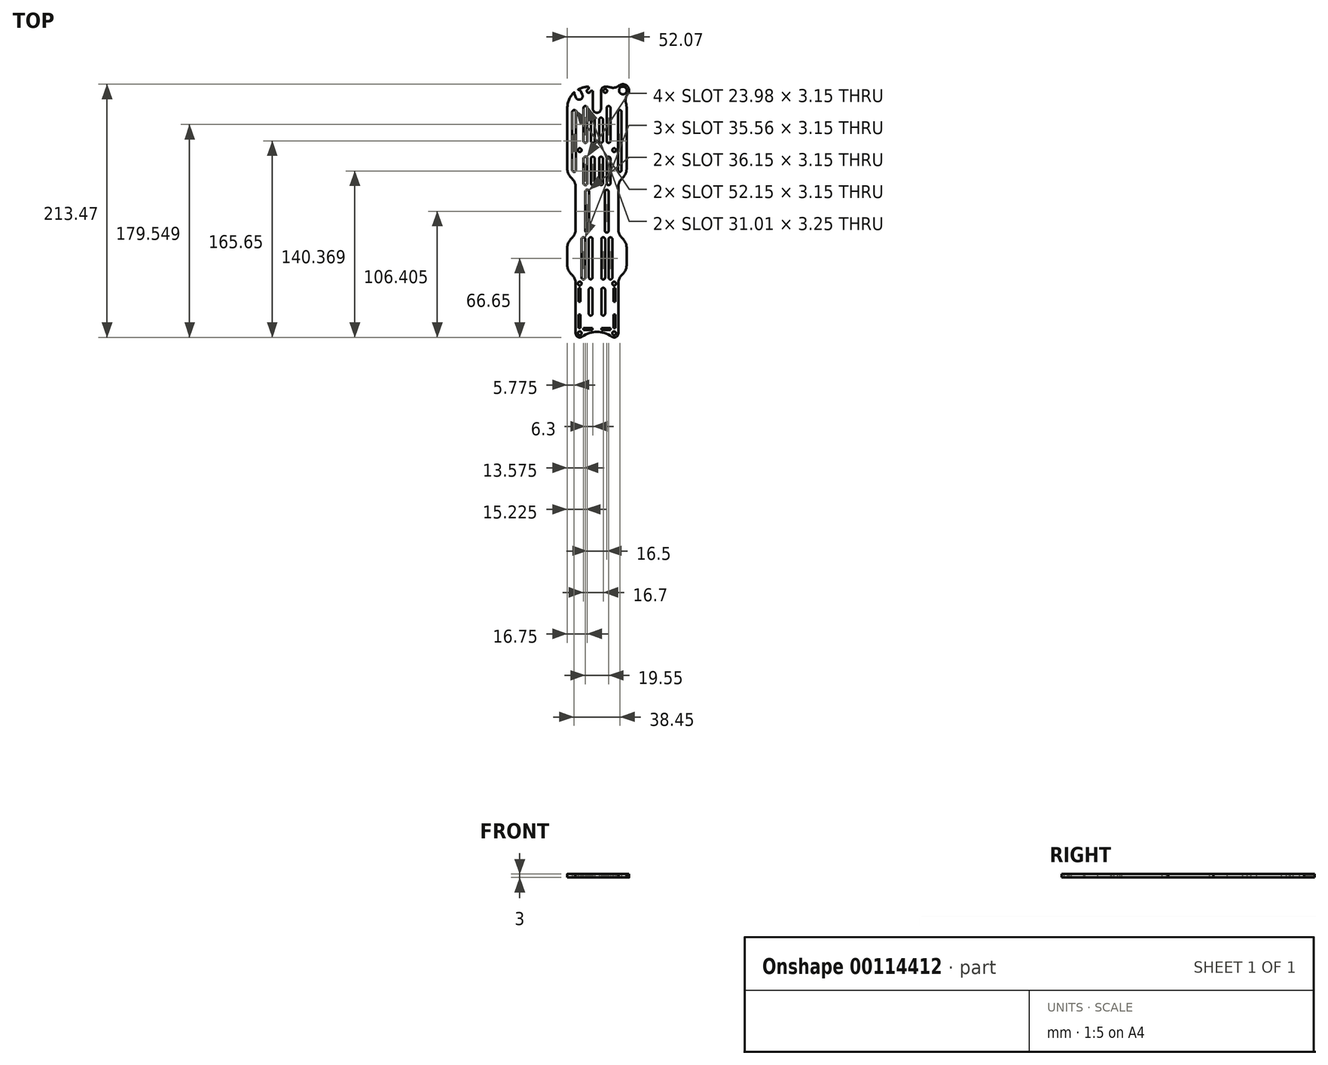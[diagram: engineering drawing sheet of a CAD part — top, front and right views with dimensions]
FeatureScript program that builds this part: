
annotation { "Feature Type Name" : "Feature", "Feature Type Description" : "" }
export const myFeature = defineFeature(function(context is Context, id is Id, definition is map)
    precondition{}
    {
        {
            var Q0;
            Q0=qCreatedBy(makeId("Top.planeOp"),FACE);
            var sketch = newSketch(context, id + "F0", { "sketchPlane" : qUnion([Q0])});
            skLineSegment(sketch, "E0.bottom", {"start": v(16.5, 48.3) * mm, "end": v(0, 48.3) * mm});
            skLineSegment(sketch, "E0.top", {"start": v(16.5, 15.3) * mm, "end": v(0, 15.3) * mm});
            skLineSegment(sketch, "E0.left", {"start": v(16.5, 48.3) * mm, "end": v(16.5, 15.3) * mm});
            skLineSegment(sketch, "E1", {"start": v(25, 118.8) * mm, "end": v(25, 67.6) * mm});
            skLineSegment(sketch, "E2", {"start": v(0, 31.8) * mm, "end": v(16.5, 48.3) * mm});
            skLineSegment(sketch, "E3", {"start": v(0, 31.8) * mm, "end": v(16.5, 15.3) * mm});
            skLineSegment(sketch, "E4.bottom", {"start": v(0, -66.61) * mm, "end": v(14, -66.61) * mm});
            skLineSegment(sketch, "E4.right", {"start": v(14, -66.61) * mm, "end": v(14, -33.16) * mm});
            skLineSegment(sketch, "E5", {"start": v(14, -33.16) * mm, "end": v(15.65, -33.16) * mm});
            skLineSegment(sketch, "E6", {"start": v(15.65, -33.16) * mm, "end": v(15.65, -44.46) * mm});
            skLineSegment(sketch, "E7", {"start": v(15.65, -44.46) * mm, "end": v(14, -44.46) * mm});
            skLineSegment(sketch, "E8", {"start": v(3.78, -66.61) * mm, "end": v(3.78, -68.26) * mm});
            skLineSegment(sketch, "E9", {"start": v(3.78, -68.26) * mm, "end": v(11.43, -68.26) * mm});
            skLineSegment(sketch, "E10", {"start": v(11.43, -68.26) * mm, "end": v(11.43, -66.61) * mm});
            skLineSegment(sketch, "E11", {"start": v(14, -55.31) * mm, "end": v(15.65, -55.31) * mm});
            skLineSegment(sketch, "E12", {"start": v(14, -66.61) * mm, "end": v(15.65, -66.61) * mm});
            skLineSegment(sketch, "E13", {"start": v(15.65, -66.61) * mm, "end": v(15.65, -55.31) * mm});
            skLineSegment(sketch, "E14", {"start": v(14.5, -66.61) * mm, "end": v(14.5, -71.11) * mm});
            skCircle(sketch, "E15", {"center": v(14.5, -71.11) * mm, "radius": 1.57 * mm});
            skCircle(sketch, "E16", {"center": v(14.5, -29.26) * mm, "radius": 1.57 * mm});
            skCircle(sketch, "E17.MirrorC", {"center": v(7, 133.2) * mm, "radius": 1.57 * mm});
            skCircle(sketch, "E18", {"center": v(14.5, 83.3) * mm, "radius": 1.57 * mm});
            skArc(sketch, "E19", {"start": v(12.45, -73.95) * mm, "mid": v(16.1, -74.23) * mm, "end": v(18, -71.11) * mm});
            skLineSegment(sketch, "E20.trimOffspring", {"start": v(12.93, -71.11) * mm, "end": v(14.5, -71.11) * mm});
            skArc(sketch, "E21", {"start": v(12.45, -73.95) * mm, "mid": v(6.54, -70.96) * mm, "end": v(0, -69.93) * mm});
            skLineSegment(sketch, "E22", {"start": v(14.5, -71.11) * mm, "end": v(18, -71.11) * mm});
            skLineSegment(sketch, "E23", {"start": v(18, -71.11) * mm, "end": v(18, -29.26) * mm});
            skLineSegment(sketch, "E24.trimOffspring", {"start": v(14.5, -30.84) * mm, "end": v(14.5, -29.26) * mm});
            skLineSegment(sketch, "E25", {"start": v(7, 133.2) * mm, "end": v(7, 136.8) * mm});
            skLineSegment(sketch, "E26", {"start": v(7, 133.2) * mm, "end": v(7, 131.63) * mm});
            skArc(sketch, "E27", {"start": v(7, 136.8) * mm, "mid": v(4.46, 135.74) * mm, "end": v(3.4, 133.2) * mm});
            skLineSegment(sketch, "E28.trimOffspring", {"start": v(3.4, 133.2) * mm, "end": v(7, 133.2) * mm});
            skLineSegment(sketch, "E29", {"start": v(3.4, 133.2) * mm, "end": v(3.4, 118.2) * mm});
            skArc(sketch, "E30", {"start": v(0, 114.8) * mm, "mid": v(2.4, 115.8) * mm, "end": v(3.4, 118.2) * mm});
            skLineSegment(sketch, "E31.trimOffspring", {"start": v(0, 114.8) * mm, "end": v(0, -66.61) * mm});
            skArc(sketch, "E32", {"start": v(25, 118.8) * mm, "mid": v(24.85, 121.15) * mm, "end": v(24.38, 123.46) * mm});
            skLineSegment(sketch, "E33", {"start": v(14.5, -29.26) * mm, "end": v(16.07, -29.26) * mm});
            skArc(sketch, "E34", {"start": v(18, -29.26) * mm, "mid": v(18.92, -24.99) * mm, "end": v(21.5, -21.46) * mm});
            skArc(sketch, "E35", {"start": v(21.5, -21.46) * mm, "mid": v(24.08, -17.94) * mm, "end": v(25, -13.66) * mm});
            skLineSegment(sketch, "E36", {"start": v(25, -13.66) * mm, "end": v(25, 1) * mm});
            skArc(sketch, "E37", {"start": v(25, 1) * mm, "mid": v(24.08, 5.27) * mm, "end": v(21.5, 8.8) * mm});
            skArc(sketch, "E38", {"start": v(21.5, 8.8) * mm, "mid": v(19.18, 11.74) * mm, "end": v(18, 15.3) * mm});
            skArc(sketch, "E39", {"start": v(25, 67.6) * mm, "mid": v(24.08, 63.32) * mm, "end": v(21.5, 59.8) * mm});
            skArc(sketch, "E40", {"start": v(21.5, 59.8) * mm, "mid": v(19.18, 56.85) * mm, "end": v(18, 53.3) * mm});
            skLineSegment(sketch, "E41.trimOffspring", {"start": v(14.5, 48.3) * mm, "end": v(14.5, 84.87) * mm});
            skLineSegment(sketch, "E42.trimOffspring", {"start": v(18, 15.3) * mm, "end": v(18, 53.3) * mm});
            skLineSegment(sketch, "E43", {"start": v(5.05, 109.08) * mm, "end": v(5.05, 91) * mm});
            skLineSegment(sketch, "E44", {"start": v(1.9, 109.08) * mm, "end": v(1.9, 91) * mm});
            skLineSegment(sketch, "E45", {"start": v(20.8, 66.54) * mm, "end": v(17.65, 66.54) * mm});
            skCircle(sketch, "E46", {"center": v(19.22, 66.54) * mm, "radius": 1.58 * mm});
            skLineSegment(sketch, "E47", {"start": v(14.5, -29.26) * mm, "end": v(0, -29.26) * mm});
            skLineSegment(sketch, "E48", {"start": v(20.8, 66.54) * mm, "end": v(20.8, 115.54) * mm});
            skLineSegment(sketch, "E49", {"start": v(17.65, 66.54) * mm, "end": v(17.65, 115.54) * mm});
            skLineSegment(sketch, "E50", {"start": v(11.35, 62.93) * mm, "end": v(11.35, 76.17) * mm});
            skLineSegment(sketch, "E51", {"start": v(8.2, 62.93) * mm, "end": v(8.2, 76.17) * mm});
            skLineSegment(sketch, "E52", {"start": v(20.8, 115.54) * mm, "end": v(17.65, 115.54) * mm});
            skLineSegment(sketch, "E53", {"start": v(6.85, -54.61) * mm, "end": v(6.85, -34.36) * mm});
            skLineSegment(sketch, "E54", {"start": v(3.7, -54.61) * mm, "end": v(3.7, -34.36) * mm});
            skLineSegment(sketch, "E55.trimOffspring", {"start": v(3.7, -54.61) * mm, "end": v(6.85, -54.61) * mm});
            skCircle(sketch, "E56", {"center": v(5.28, -54.61) * mm, "radius": 1.57 * mm});
            skLineSegment(sketch, "E57", {"start": v(3.7, 8.24) * mm, "end": v(6.85, 8.24) * mm});
            skCircle(sketch, "E58", {"center": v(5.28, 8.24) * mm, "radius": 1.57 * mm});
            skLineSegment(sketch, "E59.trimOffspring", {"start": v(8.2, 91) * mm, "end": v(11.35, 91) * mm});
            skLineSegment(sketch, "E60.trimOffspring", {"start": v(1.9, 91) * mm, "end": v(5.05, 91) * mm});
            skPoint(sketch, "E61", {"position": v(3.47, 91) * mm});
            skPoint(sketch, "E62", {"position": v(9.77, 91) * mm});
            skCircle(sketch, "E63", {"center": v(3.47, 91) * mm, "radius": 1.58 * mm});
            skLineSegment(sketch, "E64.trimOffspring", {"start": v(1.9, 76.17) * mm, "end": v(1.9, 62.93) * mm});
            skLineSegment(sketch, "E65.trimOffspring", {"start": v(5.05, 76.17) * mm, "end": v(5.05, 62.93) * mm});
            skLineSegment(sketch, "E66.trimOffspring", {"start": v(8.2, 91) * mm, "end": v(8.2, 119.29) * mm});
            skLineSegment(sketch, "E67.trimOffspring", {"start": v(11.35, 91) * mm, "end": v(11.35, 119.29) * mm});
            skCircle(sketch, "E68", {"center": v(9.77, 91) * mm, "radius": 1.57 * mm});
            skCircle(sketch, "E69", {"center": v(19.22, 115.54) * mm, "radius": 1.57 * mm});
            skLineSegment(sketch, "E70.MirrorCS", {"start": v(13, 8.24) * mm, "end": v(13, -24.16) * mm});
            skLineSegment(sketch, "E71.MirrorCS", {"start": v(9.85, 8.24) * mm, "end": v(9.85, -24.16) * mm});
            skLineSegment(sketch, "E72.trimOffspring", {"start": v(0, 1) * mm, "end": v(25, 1) * mm});
            skLineSegment(sketch, "E73.trimOffspring", {"start": v(0, -13.66) * mm, "end": v(25, -13.66) * mm});
            skLineSegment(sketch, "E74.trimOffspring", {"start": v(0, -33.16) * mm, "end": v(14, -33.16) * mm});
            skLineSegment(sketch, "E75", {"start": v(1.9, 109.08) * mm, "end": v(5.05, 109.08) * mm});
            skCircle(sketch, "E76", {"center": v(3.47, 109.08) * mm, "radius": 1.57 * mm});
            skLineSegment(sketch, "E77", {"start": v(8.2, 118.8) * mm, "end": v(11.35, 118.8) * mm});
            skCircle(sketch, "E78", {"center": v(9.77, 118.8) * mm, "radius": 1.65 * mm});
            skLineSegment(sketch, "E79", {"start": v(8.2, 76.17) * mm, "end": v(11.35, 76.17) * mm});
            skLineSegment(sketch, "E80", {"start": v(5.05, 76.17) * mm, "end": v(1.9, 76.17) * mm});
            skCircle(sketch, "E81", {"center": v(3.47, 76.17) * mm, "radius": 1.58 * mm});
            skCircle(sketch, "E82", {"center": v(9.77, 76.17) * mm, "radius": 1.57 * mm});
            skLineSegment(sketch, "E83", {"start": v(5.05, 62.93) * mm, "end": v(5.05, 55.35) * mm});
            skLineSegment(sketch, "E84", {"start": v(8.2, 55.35) * mm, "end": v(11.35, 55.35) * mm});
            skLineSegment(sketch, "E85", {"start": v(5.05, 55.35) * mm, "end": v(1.9, 55.35) * mm});
            skLineSegment(sketch, "E86", {"start": v(1.9, 62.93) * mm, "end": v(1.9, 55.35) * mm});
            skLineSegment(sketch, "E87", {"start": v(11.35, 62.93) * mm, "end": v(11.35, 55.35) * mm});
            skLineSegment(sketch, "E88", {"start": v(8.2, 62.93) * mm, "end": v(8.2, 55.35) * mm});
            skCircle(sketch, "E89", {"center": v(9.77, 55.35) * mm, "radius": 1.57 * mm});
            skCircle(sketch, "E90", {"center": v(3.47, 55.35) * mm, "radius": 1.58 * mm});
            skLineSegment(sketch, "E91.MirrorCS", {"start": v(-12.92, -71.11) * mm, "end": v(-14.5, -71.11) * mm});
            skLineSegment(sketch, "E92.MirrorCS", {"start": v(-7, 133.2) * mm, "end": v(-7, 136.8) * mm});
            skLineSegment(sketch, "E93.MirrorCS", {"start": v(-14.5, -71.11) * mm, "end": v(-18, -71.11) * mm});
            skCircle(sketch, "E94.MirrorC", {"center": v(-14.5, -71.11) * mm, "radius": 1.57 * mm});
            skLineSegment(sketch, "E95.MirrorCS", {"start": v(-14.5, -66.61) * mm, "end": v(-14.5, -71.11) * mm});
            skLineSegment(sketch, "E96.MirrorCS", {"start": v(-14, -33.16) * mm, "end": v(-15.65, -33.16) * mm});
            skLineSegment(sketch, "E97.MirrorCS", {"start": v(-14, -66.61) * mm, "end": v(-15.65, -66.61) * mm});
            skLineSegment(sketch, "E98.MirrorCS", {"start": v(-11.42, -68.26) * mm, "end": v(-11.42, -66.61) * mm});
            skLineSegment(sketch, "E99.MirrorCS", {"start": v(-3.4, 133.2) * mm, "end": v(-7, 133.2) * mm});
            skArc(sketch, "E100.MirrorCS", {"start": v(-12.45, -73.95) * mm, "mid": v(-16.1, -74.23) * mm, "end": v(-18, -71.11) * mm});
            skArc(sketch, "E101.MirrorCS", {"start": v(-7, 136.8) * mm, "mid": v(-4.46, 135.74) * mm, "end": v(-3.4, 133.2) * mm});
            skLineSegment(sketch, "E102.MirrorCS", {"start": v(-7, 133.2) * mm, "end": v(-7, 131.63) * mm});
            skLineSegment(sketch, "E103.MirrorCS", {"start": v(-14.5, -29.26) * mm, "end": v(-16.07, -29.26) * mm});
            skLineSegment(sketch, "E104.MirrorCS", {"start": v(-14.5, -30.84) * mm, "end": v(-14.5, -29.26) * mm});
            skCircle(sketch, "E105.MirrorC", {"center": v(-7, 133.2) * mm, "radius": 1.57 * mm});
            skLineSegment(sketch, "E106.MirrorCS", {"start": v(-8.2, 118.8) * mm, "end": v(-11.35, 118.8) * mm});
            skCircle(sketch, "E107.MirrorC", {"center": v(-14.5, -29.26) * mm, "radius": 1.57 * mm});
            skLineSegment(sketch, "E108.MirrorCS", {"start": v(-3.7, -54.61) * mm, "end": v(-6.85, -54.61) * mm});
            skLineSegment(sketch, "E109.MirrorCS", {"start": v(-3.4, 133.2) * mm, "end": v(-3.4, 118.2) * mm});
            skLineSegment(sketch, "E110.MirrorCS", {"start": v(-1.9, 91) * mm, "end": v(-5.05, 91) * mm});
            skLineSegment(sketch, "E111.MirrorCS", {"start": v(-20.8, 66.54) * mm, "end": v(-17.65, 66.54) * mm});
            skLineSegment(sketch, "E112.MirrorCS", {"start": v(-8.2, 91) * mm, "end": v(-11.35, 91) * mm});
            skCircle(sketch, "E113.MirrorC", {"center": v(-9.77, 118.8) * mm, "radius": 1.65 * mm});
            skLineSegment(sketch, "E114.MirrorCS", {"start": v(-3.7, 8.24) * mm, "end": v(-6.85, 8.24) * mm});
            skLineSegment(sketch, "E115.MirrorCS", {"start": v(-5.05, 55.35) * mm, "end": v(-1.9, 55.35) * mm});
            skCircle(sketch, "E116.MirrorC", {"center": v(-5.27, -54.61) * mm, "radius": 1.57 * mm});
            skLineSegment(sketch, "E117.MirrorCS", {"start": v(-8.2, 55.35) * mm, "end": v(-11.35, 55.35) * mm});
            skCircle(sketch, "E118.MirrorC", {"center": v(-3.47, 91) * mm, "radius": 1.58 * mm});
            skArc(sketch, "E119.MirrorCS", {"start": v(-12.45, -73.95) * mm, "mid": v(-6.54, -70.96) * mm, "end": v(0, -69.93) * mm});
            skCircle(sketch, "E120.MirrorC", {"center": v(-19.22, 66.54) * mm, "radius": 1.58 * mm});
            skArc(sketch, "E121.MirrorCS", {"start": v(-21.5, 8.8) * mm, "mid": v(-19.18, 11.74) * mm, "end": v(-18, 15.3) * mm});
            skLineSegment(sketch, "E122.MirrorCS", {"start": v(-5.05, 62.93) * mm, "end": v(-5.05, 55.35) * mm});
            skLineSegment(sketch, "E123.MirrorCS", {"start": v(-3.77, -68.26) * mm, "end": v(-11.42, -68.26) * mm});
            skLineSegment(sketch, "E124.MirrorCS", {"start": v(-3.77, -66.61) * mm, "end": v(-3.77, -68.26) * mm});
            skLineSegment(sketch, "E125.MirrorCS", {"start": v(0, -66.61) * mm, "end": v(-14, -66.61) * mm});
            skCircle(sketch, "E126.MirrorC", {"center": v(-9.77, 55.35) * mm, "radius": 1.57 * mm});
            skArc(sketch, "E127.MirrorCS", {"start": v(-25, 1) * mm, "mid": v(-24.08, 5.27) * mm, "end": v(-21.5, 8.8) * mm});
            skLineSegment(sketch, "E128.MirrorCS", {"start": v(-8.2, 62.93) * mm, "end": v(-8.2, 55.35) * mm});
            skArc(sketch, "E129.MirrorCS", {"start": v(-18, -29.26) * mm, "mid": v(-18.92, -24.99) * mm, "end": v(-21.5, -21.46) * mm});
            skLineSegment(sketch, "E130.MirrorCS", {"start": v(-8.2, 76.17) * mm, "end": v(-11.35, 76.17) * mm});
            skLineSegment(sketch, "E131.MirrorCS", {"start": v(-5.05, 76.17) * mm, "end": v(-1.9, 76.17) * mm});
            skLineSegment(sketch, "E132.MirrorCS", {"start": v(-11.35, 62.93) * mm, "end": v(-11.35, 55.35) * mm});
            skCircle(sketch, "E133.MirrorC", {"center": v(-9.77, 91) * mm, "radius": 1.57 * mm});
            skCircle(sketch, "E134.MirrorC", {"center": v(-5.27, 8.24) * mm, "radius": 1.57 * mm});
            skArc(sketch, "E135.MirrorCS", {"start": v(-21.5, 59.8) * mm, "mid": v(-19.18, 56.85) * mm, "end": v(-18, 53.3) * mm});
            skArc(sketch, "E136.MirrorCS", {"start": v(0, 114.8) * mm, "mid": v(-2.4, 115.8) * mm, "end": v(-3.4, 118.2) * mm});
            skArc(sketch, "E137.MirrorCS", {"start": v(-25, 67.6) * mm, "mid": v(-24.08, 63.32) * mm, "end": v(-21.5, 59.8) * mm});
            skLineSegment(sketch, "E138.MirrorCS", {"start": v(-1.9, 109.08) * mm, "end": v(-5.05, 109.08) * mm});
            skLineSegment(sketch, "E139.MirrorCS", {"start": v(-15.65, -66.61) * mm, "end": v(-15.65, -55.31) * mm});
            skCircle(sketch, "E140.MirrorC", {"center": v(-3.47, 55.35) * mm, "radius": 1.58 * mm});
            skLineSegment(sketch, "E141.MirrorCS", {"start": v(-15.65, -44.46) * mm, "end": v(-14, -44.46) * mm});
            skLineSegment(sketch, "E142.MirrorCS", {"start": v(-15.65, -33.16) * mm, "end": v(-15.65, -44.46) * mm});
            skLineSegment(sketch, "E143.MirrorCS", {"start": v(-14, -66.61) * mm, "end": v(-14, -33.16) * mm});
            skLineSegment(sketch, "E144.MirrorCS", {"start": v(-14, -55.31) * mm, "end": v(-15.65, -55.31) * mm});
            skCircle(sketch, "E145.MirrorC", {"center": v(-9.77, 76.17) * mm, "radius": 1.57 * mm});
            skArc(sketch, "E146.MirrorCS", {"start": v(-21.5, -21.46) * mm, "mid": v(-24.08, -17.94) * mm, "end": v(-25, -13.66) * mm});
            skCircle(sketch, "E147.MirrorC", {"center": v(-3.47, 76.17) * mm, "radius": 1.58 * mm});
            skLineSegment(sketch, "E148.MirrorCS", {"start": v(-25, -13.66) * mm, "end": v(-25, 1) * mm});
            skLineSegment(sketch, "E149.MirrorCS", {"start": v(-20.8, 115.54) * mm, "end": v(-17.65, 115.54) * mm});
            skCircle(sketch, "E150.MirrorC", {"center": v(-19.22, 115.54) * mm, "radius": 1.57 * mm});
            skCircle(sketch, "E151.MirrorC", {"center": v(-14.5, 83.3) * mm, "radius": 1.57 * mm});
            skLineSegment(sketch, "E152.MirrorCS", {"start": v(-11.35, 62.93) * mm, "end": v(-11.35, 76.17) * mm});
            skLineSegment(sketch, "E153.MirrorCS", {"start": v(-8.2, 62.93) * mm, "end": v(-8.2, 76.17) * mm});
            skLineSegment(sketch, "E154.MirrorCS", {"start": v(-1.9, 62.93) * mm, "end": v(-1.9, 55.35) * mm});
            skLineSegment(sketch, "E155.MirrorCS", {"start": v(-14.5, 48.3) * mm, "end": v(-14.5, 84.87) * mm});
            skLineSegment(sketch, "E156.MirrorCS", {"start": v(-5.05, 76.17) * mm, "end": v(-5.05, 62.93) * mm});
            skLineSegment(sketch, "E157.MirrorCS", {"start": v(-18, -71.11) * mm, "end": v(-18, -29.26) * mm});
            skLineSegment(sketch, "E158.MirrorCS", {"start": v(-1.9, 76.17) * mm, "end": v(-1.9, 62.93) * mm});
            skCircle(sketch, "E159.MirrorC", {"center": v(-3.47, 109.08) * mm, "radius": 1.57 * mm});
            skLineSegment(sketch, "E160.MirrorCS", {"start": v(0, 1) * mm, "end": v(-25, 1) * mm});
            skLineSegment(sketch, "E161.MirrorCS", {"start": v(-14.5, -29.26) * mm, "end": v(0, -29.26) * mm});
            skLineSegment(sketch, "E162.MirrorCS", {"start": v(-3.7, -54.61) * mm, "end": v(-3.7, -34.36) * mm});
            skLineSegment(sketch, "E163.MirrorCS", {"start": v(-9.85, 8.24) * mm, "end": v(-9.85, -24.16) * mm});
            skLineSegment(sketch, "E164.MirrorCS", {"start": v(0, -33.16) * mm, "end": v(-14, -33.16) * mm});
            skLineSegment(sketch, "E165.MirrorCS", {"start": v(-16.5, 15.3) * mm, "end": v(0, 15.3) * mm});
            skLineSegment(sketch, "E166.MirrorCS", {"start": v(-13, 8.24) * mm, "end": v(-13, -24.16) * mm});
            skLineSegment(sketch, "E167.MirrorCS", {"start": v(0, -13.66) * mm, "end": v(-25, -13.66) * mm});
            skLineSegment(sketch, "E168.MirrorCS", {"start": v(-18, 15.3) * mm, "end": v(-18, 53.3) * mm});
            skArc(sketch, "E169.MirrorCS", {"start": v(-25, 118.8) * mm, "mid": v(-23.5, 125.98) * mm, "end": v(-19.27, 131.97) * mm});
            skLineSegment(sketch, "E170.MirrorCS", {"start": v(0, 31.8) * mm, "end": v(-16.5, 15.3) * mm});
            skLineSegment(sketch, "E171.MirrorCS", {"start": v(0, 31.8) * mm, "end": v(-16.5, 48.3) * mm});
            skLineSegment(sketch, "E172.MirrorCS", {"start": v(-25, 118.8) * mm, "end": v(-25, 67.6) * mm});
            skLineSegment(sketch, "E173.MirrorCS", {"start": v(-16.5, 48.3) * mm, "end": v(-16.5, 15.3) * mm});
            skLineSegment(sketch, "E174.MirrorCS", {"start": v(-16.5, 48.3) * mm, "end": v(0, 48.3) * mm});
            skLineSegment(sketch, "E175.MirrorCS", {"start": v(-1.9, 109.08) * mm, "end": v(-1.9, 91) * mm});
            skLineSegment(sketch, "E176.MirrorCS", {"start": v(-6.85, -54.61) * mm, "end": v(-6.85, -34.36) * mm});
            skLineSegment(sketch, "E177.MirrorCS", {"start": v(-5.05, 109.08) * mm, "end": v(-5.05, 91) * mm});
            skLineSegment(sketch, "E178.MirrorCS", {"start": v(-11.35, 91) * mm, "end": v(-11.35, 119.29) * mm});
            skLineSegment(sketch, "E179.MirrorCS", {"start": v(-8.2, 91) * mm, "end": v(-8.2, 119.29) * mm});
            skLineSegment(sketch, "E180.MirrorCS", {"start": v(-20.8, 66.54) * mm, "end": v(-20.8, 115.54) * mm});
            skLineSegment(sketch, "E181.MirrorCS", {"start": v(-17.65, 66.54) * mm, "end": v(-17.65, 115.54) * mm});
            skArc(sketch, "E182", {"start": v(-13.23, 132.27) * mm, "mid": v(-14.21, 133.52) * mm, "end": v(-15.7, 134.1) * mm});
            skArc(sketch, "E183", {"start": v(-17.8, 127.65) * mm, "mid": v(-13.87, 126.04) * mm, "end": v(-12.27, 129.97) * mm});
            skLineSegment(sketch, "E184", {"start": v(-12.27, 129.97) * mm, "end": v(-13.23, 132.27) * mm});
            skLineSegment(sketch, "E185", {"start": v(-18.77, 129.96) * mm, "end": v(-17.8, 127.65) * mm});
            skPoint(sketch, "E186", {"position": v(-18.92, 131.79) * mm});
            skPoint(sketch, "E187", {"position": v(-15.7, 134.1) * mm});
            skArc(sketch, "E188.trimOffspring", {"start": v(-18.92, 131.79) * mm, "mid": v(-18.99, 130.86) * mm, "end": v(-18.77, 129.96) * mm});
            skArc(sketch, "E189.trimOffspring", {"start": v(-15.82, 134.48) * mm, "mid": v(-11.56, 136.2) * mm, "end": v(-7, 136.8) * mm});
            skArc(sketch, "E190", {"start": v(-15.7, 134.1) * mm, "mid": v(-15.88, 134.25) * mm, "end": v(-15.82, 134.48) * mm});
            skArc(sketch, "E191", {"start": v(-18.92, 131.79) * mm, "mid": v(-19.03, 132) * mm, "end": v(-19.27, 131.97) * mm});
            skLineSegment(sketch, "E192", {"start": v(13, 8.24) * mm, "end": v(9.85, 8.24) * mm});
            skLineSegment(sketch, "E193", {"start": v(-9.85, 8.24) * mm, "end": v(-13, 8.24) * mm});
            skLineSegment(sketch, "E194", {"start": v(13, -24.16) * mm, "end": v(9.85, -24.16) * mm});
            skLineSegment(sketch, "E195", {"start": v(-9.85, -24.16) * mm, "end": v(-13, -24.16) * mm});
            skCircle(sketch, "E196", {"center": v(11.43, -24.16) * mm, "radius": 1.57 * mm});
            skCircle(sketch, "E197", {"center": v(11.43, 8.24) * mm, "radius": 1.57 * mm});
            skCircle(sketch, "E198", {"center": v(-11.42, 8.24) * mm, "radius": 1.58 * mm});
            skCircle(sketch, "E199", {"center": v(-11.42, -24.16) * mm, "radius": 1.58 * mm});
            skLineSegment(sketch, "E200", {"start": v(7, 118.8) * mm, "end": v(21.85, 133.64) * mm});
            skLineSegment(sketch, "E201", {"start": v(21.85, 133.64) * mm, "end": v(25.54, 137.33) * mm});
            skCircle(sketch, "E202", {"center": v(21.85, 133.64) * mm, "radius": 3.25 * mm});
            skCircle(sketch, "E203", {"center": v(21.85, 133.64) * mm, "radius": 5.22 * mm});
            skLineSegment(sketch, "E204", {"start": v(21.85, 133.64) * mm, "end": v(24.15, 131.35) * mm});
            skLineSegment(sketch, "E205", {"start": v(21.85, 133.64) * mm, "end": v(19.55, 135.94) * mm});
            skArc(sketch, "E206.trimOffspring", {"start": v(11.67, 136.18) * mm, "mid": v(9.36, 136.64) * mm, "end": v(7, 136.8) * mm});
            skArc(sketch, "E207", {"start": v(11.67, 136.18) * mm, "mid": v(15.04, 136.03) * mm, "end": v(18.16, 137.33) * mm});
            skArc(sketch, "E208", {"start": v(24.38, 123.46) * mm, "mid": v(24.24, 126.84) * mm, "end": v(25.54, 129.95) * mm});
            skLineSegment(sketch, "E209", {"start": v(-6.85, -24.16) * mm, "end": v(-3.7, -24.16) * mm});
            skLineSegment(sketch, "E210.trimOffspring", {"start": v(3.7, -24.16) * mm, "end": v(6.85, -24.16) * mm});
            skCircle(sketch, "E211", {"center": v(-5.27, -24.16) * mm, "radius": 1.5 * mm});
            skCircle(sketch, "E212", {"center": v(5.28, -24.16) * mm, "radius": 1.57 * mm});
            skLineSegment(sketch, "E213", {"start": v(-6.85, -34.36) * mm, "end": v(-3.7, -34.36) * mm});
            skLineSegment(sketch, "E214.trimOffspring", {"start": v(-6.85, -24.16) * mm, "end": v(-6.85, 8.24) * mm});
            skLineSegment(sketch, "E215.trimOffspring", {"start": v(-3.7, -24.16) * mm, "end": v(-3.7, 8.24) * mm});
            skLineSegment(sketch, "E216.trimOffspring", {"start": v(6.85, -24.16) * mm, "end": v(6.85, 8.24) * mm});
            skLineSegment(sketch, "E217.trimOffspring", {"start": v(3.7, -24.16) * mm, "end": v(3.7, 8.24) * mm});
            skLineSegment(sketch, "E218.trimOffspring", {"start": v(3.7, -34.36) * mm, "end": v(6.85, -34.36) * mm});
            skCircle(sketch, "E219", {"center": v(-5.27, -34.36) * mm, "radius": 1.57 * mm});
            skCircle(sketch, "E220", {"center": v(5.28, -34.36) * mm, "radius": 1.57 * mm});
            skLineSegment(sketch, "E221", {"start": v(-8.25, 48.3) * mm, "end": v(-8.25, 15.3) * mm});
            skLineSegment(sketch, "E222", {"start": v(8.25, 48.3) * mm, "end": v(8.25, 15.3) * mm});
            skCircle(sketch, "E223", {"center": v(8.25, 48.3) * mm, "radius": 1.57 * mm});
            skCircle(sketch, "E224", {"center": v(8.25, 15.3) * mm, "radius": 1.57 * mm});
            skCircle(sketch, "E225", {"center": v(-8.25, 15.3) * mm, "radius": 1.57 * mm});
            skCircle(sketch, "E226", {"center": v(-8.25, 48.3) * mm, "radius": 1.57 * mm});
            skLineSegment(sketch, "E227", {"start": v(-9.82, 48.3) * mm, "end": v(-9.82, 15.3) * mm});
            skLineSegment(sketch, "E228", {"start": v(-6.67, 15.3) * mm, "end": v(-6.67, 48.3) * mm});
            skLineSegment(sketch, "E229", {"start": v(6.68, 48.3) * mm, "end": v(6.68, 15.3) * mm});
            skLineSegment(sketch, "E230", {"start": v(9.83, 15.3) * mm, "end": v(9.83, 48.3) * mm});
            skSolve(sketch);
        }
        {
            var Q0;
            {var subQ0=sQuery(id+"F0.wireOp",EDGE,"E174.MirrorCS");var subQ5=makeQuery(id+"F0.imprint","IMPRINT",VERTEX,{"derivedFrom":subQ0});Q0=makeQuery(id+"F0.imprint","IMPRINT",FACE,{"disambiguationData":[TD([[makeQuery(id+"F0.imprint","IMPRINT",EDGE,{"disambiguationData":[TD([[subQ5,1.0]])],"derivedFrom":subQ0}),-1.0]])]});}
            var Q1;
            {var subQ3=sQuery(id+"F0.wireOp",EDGE,"E171.MirrorCS");var subQ5=sQuery(id+"F0.wireOp",EDGE,"E228");var subQ6=makeQuery(id+"F0.imprint","INTERSECT",VERTEX,{"derivedFrom":[subQ3,subQ5]});Q1=makeQuery(id+"F0.imprint","IMPRINT",FACE,{"disambiguationData":[TD([[makeQuery(id+"F0.imprint","IMPRINT",EDGE,{"disambiguationData":[TD([[subQ6,-1.0]])],"derivedFrom":subQ5}),-1.0]])]});}
            var Q2;
            {var subQ0=sQuery(id+"F0.wireOp",EDGE,"E148.MirrorCS");Q2=makeQuery(id+"F0.imprint","IMPRINT",FACE,{"disambiguationData":[TD([[makeQuery(id+"F0.imprint","IMPRINT",EDGE,{"derivedFrom":subQ0}),-1.0]])]});}
            var Q3;
            {var subQ0=sQuery(id+"F0.wireOp",EDGE,"E214.trimOffspring");var subQ1=sQuery(id+"F0.wireOp",EDGE,"E160.MirrorCS");var subQ2=makeQuery(id+"F0.imprint","INTERSECT",VERTEX,{"derivedFrom":[subQ1,subQ0]});Q3=makeQuery(id+"F0.imprint","IMPRINT",FACE,{"disambiguationData":[TD([[makeQuery(id+"F0.imprint","IMPRINT",EDGE,{"disambiguationData":[TD([[subQ2,-1.0]])],"derivedFrom":subQ1}),1.0]])]});}
            var Q4;
            {var subQ5=sQuery(id+"F0.wireOp",EDGE,"E27");Q4=makeQuery(id+"F0.imprint","IMPRINT",FACE,{"disambiguationData":[TD([[makeQuery(id+"F0.imprint","IMPRINT",EDGE,{"derivedFrom":subQ5}),1.0]])]});}
            var Q5;
            {var subQ0=sQuery(id+"F0.wireOp",EDGE,"E0.left");Q5=makeQuery(id+"F0.imprint","IMPRINT",FACE,{"disambiguationData":[TD([[makeQuery(id+"F0.imprint","IMPRINT",EDGE,{"derivedFrom":subQ0}),-1.0]])]});}
            var Q6;
            {var subQ0=sQuery(id+"F0.wireOp",EDGE,"E3");var subQ3=sQuery(id+"F0.wireOp",EDGE,"E230");var subQ5=makeQuery(id+"F0.imprint","INTERSECT",VERTEX,{"derivedFrom":[subQ0,subQ3]});Q6=makeQuery(id+"F0.imprint","IMPRINT",FACE,{"disambiguationData":[TD([[makeQuery(id+"F0.imprint","IMPRINT",EDGE,{"disambiguationData":[TD([[subQ5,-1.0]])],"derivedFrom":subQ0}),-1.0]])]});}
            var Q7;
            {var subQ22=sQuery(id+"F0.wireOp",EDGE,"E5");Q7=makeQuery(id+"F0.imprint","IMPRINT",FACE,{"disambiguationData":[TD([[makeQuery(id+"F0.imprint","IMPRINT",EDGE,{"derivedFrom":subQ22}),1.0]])]});}
            var Q8;
            {var subQ23=sQuery(id+"F0.wireOp",EDGE,"E8");Q8=makeQuery(id+"F0.imprint","IMPRINT",FACE,{"disambiguationData":[TD([[makeQuery(id+"F0.imprint","IMPRINT",EDGE,{"derivedFrom":subQ23}),-1.0]])]});}
            var Q9;
            {var subQ2=sQuery(id+"F0.wireOp",EDGE,"E53");Q9=makeQuery(id+"F0.imprint","IMPRINT",FACE,{"disambiguationData":[TD([[makeQuery(id+"F0.imprint","IMPRINT",EDGE,{"derivedFrom":subQ2}),-1.0]])]});}
            var Q10;
            {var subQ2=sQuery(id+"F0.wireOp",EDGE,"E53");Q10=makeQuery(id+"F0.imprint","IMPRINT",FACE,{"disambiguationData":[TD([[makeQuery(id+"F0.imprint","IMPRINT",EDGE,{"derivedFrom":subQ2}),-1.0]])]});}
            var Q11;
            {var subQ22=sQuery(id+"F0.wireOp",EDGE,"E5");Q11=makeQuery(id+"F0.imprint","IMPRINT",FACE,{"disambiguationData":[TD([[makeQuery(id+"F0.imprint","IMPRINT",EDGE,{"derivedFrom":subQ22}),1.0]])]});}
            var Q12;
            {var subQ1=sQuery(id+"F0.wireOp",EDGE,"E0.bottom");var subQ3=makeQuery(id+"F0.imprint","IMPRINT",VERTEX,{"derivedFrom":subQ1});Q12=makeQuery(id+"F0.imprint","IMPRINT",FACE,{"disambiguationData":[TD([[makeQuery(id+"F0.imprint","IMPRINT",EDGE,{"disambiguationData":[TD([[subQ3,1.0]])],"derivedFrom":subQ1}),1.0]])]});}
            var Q13;
            {var subQ3=sQuery(id+"F0.wireOp",EDGE,"E229");var subQ5=sQuery(id+"F0.wireOp",EDGE,"E2");var subQ7=makeQuery(id+"F0.imprint","INTERSECT",VERTEX,{"derivedFrom":[subQ5,subQ3]});Q13=makeQuery(id+"F0.imprint","IMPRINT",FACE,{"disambiguationData":[TD([[makeQuery(id+"F0.imprint","IMPRINT",EDGE,{"disambiguationData":[TD([[subQ7,1.0]])],"derivedFrom":subQ3}),-1.0]])]});}
            var Q14;
            {var subQ1=sQuery(id+"F0.wireOp",EDGE,"E0.bottom");var subQ3=makeQuery(id+"F0.imprint","IMPRINT",VERTEX,{"derivedFrom":subQ1});Q14=makeQuery(id+"F0.imprint","IMPRINT",FACE,{"disambiguationData":[TD([[makeQuery(id+"F0.imprint","IMPRINT",EDGE,{"disambiguationData":[TD([[subQ3,1.0]])],"derivedFrom":subQ1}),1.0]])]});}
            var Q15;
            {var subQ3=sQuery(id+"F0.wireOp",EDGE,"E229");var subQ5=sQuery(id+"F0.wireOp",EDGE,"E2");var subQ7=makeQuery(id+"F0.imprint","INTERSECT",VERTEX,{"derivedFrom":[subQ5,subQ3]});Q15=makeQuery(id+"F0.imprint","IMPRINT",FACE,{"disambiguationData":[TD([[makeQuery(id+"F0.imprint","IMPRINT",EDGE,{"disambiguationData":[TD([[subQ7,1.0]])],"derivedFrom":subQ3}),-1.0]])]});}
            var Q16;
            {var subQ0=sQuery(id+"F0.wireOp",EDGE,"E36");Q16=makeQuery(id+"F0.imprint","IMPRINT",FACE,{"disambiguationData":[TD([[makeQuery(id+"F0.imprint","IMPRINT",EDGE,{"derivedFrom":subQ0}),1.0]])]});}
            var Q17;
            {var subQ2=sQuery(id+"F0.wireOp",EDGE,"E53");Q17=makeQuery(id+"F0.imprint","IMPRINT",FACE,{"disambiguationData":[TD([[makeQuery(id+"F0.imprint","IMPRINT",EDGE,{"derivedFrom":subQ2}),-1.0]])]});}
            var Q18;
            {var subQ2=sQuery(id+"F0.wireOp",EDGE,"E53");Q18=makeQuery(id+"F0.imprint","IMPRINT",FACE,{"disambiguationData":[TD([[makeQuery(id+"F0.imprint","IMPRINT",EDGE,{"derivedFrom":subQ2}),-1.0]])]});}
            var Q19;
            {var subQ0=sQuery(id+"F0.wireOp",EDGE,"E160.MirrorCS");var subQ5=sQuery(id+"F0.wireOp",EDGE,"E215.trimOffspring");var subQ6=makeQuery(id+"F0.imprint","INTERSECT",VERTEX,{"derivedFrom":[subQ0,subQ5]});Q19=makeQuery(id+"F0.imprint","IMPRINT",FACE,{"disambiguationData":[TD([[makeQuery(id+"F0.imprint","IMPRINT",EDGE,{"disambiguationData":[TD([[subQ6,1.0]])],"derivedFrom":subQ5}),-1.0]])]});}
            var Q20;
            {var subQ1=sQuery(id+"F0.wireOp",EDGE,"E0.bottom");var subQ3=makeQuery(id+"F0.imprint","IMPRINT",VERTEX,{"derivedFrom":subQ1});Q20=makeQuery(id+"F0.imprint","IMPRINT",FACE,{"disambiguationData":[TD([[makeQuery(id+"F0.imprint","IMPRINT",EDGE,{"disambiguationData":[TD([[subQ3,1.0]])],"derivedFrom":subQ1}),1.0]])]});}
            var Q21;
            {var subQ3=sQuery(id+"F0.wireOp",EDGE,"E229");var subQ5=sQuery(id+"F0.wireOp",EDGE,"E2");var subQ7=makeQuery(id+"F0.imprint","INTERSECT",VERTEX,{"derivedFrom":[subQ5,subQ3]});Q21=makeQuery(id+"F0.imprint","IMPRINT",FACE,{"disambiguationData":[TD([[makeQuery(id+"F0.imprint","IMPRINT",EDGE,{"disambiguationData":[TD([[subQ7,1.0]])],"derivedFrom":subQ3}),-1.0]])]});}
            var Q22;
            {var subQ0=sQuery(id+"F0.wireOp",EDGE,"E72.trimOffspring");var subQ5=sQuery(id+"F0.wireOp",EDGE,"E217.trimOffspring");var subQ6=makeQuery(id+"F0.imprint","INTERSECT",VERTEX,{"derivedFrom":[subQ0,subQ5]});Q22=makeQuery(id+"F0.imprint","IMPRINT",FACE,{"disambiguationData":[TD([[makeQuery(id+"F0.imprint","IMPRINT",EDGE,{"disambiguationData":[TD([[subQ6,1.0]])],"derivedFrom":subQ5}),1.0]])]});}
            var Q23;
            {var subQ66=sQuery(id+"F0.wireOp",EDGE,"E109.MirrorCS");Q23=makeQuery(id+"F0.imprint","IMPRINT",FACE,{"disambiguationData":[TD([[makeQuery(id+"F0.imprint","IMPRINT",EDGE,{"derivedFrom":subQ66}),-1.0]])]});}
            var Q24;
            {var subQ1=sQuery(id+"F0.wireOp",EDGE,"E170.MirrorCS");var subQ3=sQuery(id+"F0.wireOp",EDGE,"E228");var subQ4=makeQuery(id+"F0.imprint","INTERSECT",VERTEX,{"derivedFrom":[subQ1,subQ3]});Q24=makeQuery(id+"F0.imprint","IMPRINT",FACE,{"disambiguationData":[TD([[makeQuery(id+"F0.imprint","IMPRINT",EDGE,{"disambiguationData":[TD([[subQ4,-1.0]])],"derivedFrom":subQ3}),-1.0]])]});}
            var Q25;
            {var subQ0=sQuery(id+"F0.wireOp",EDGE,"E170.MirrorCS");var subQ3=sQuery(id+"F0.wireOp",EDGE,"E227");var subQ5=makeQuery(id+"F0.imprint","INTERSECT",VERTEX,{"derivedFrom":[subQ0,subQ3]});Q25=makeQuery(id+"F0.imprint","IMPRINT",FACE,{"disambiguationData":[TD([[makeQuery(id+"F0.imprint","IMPRINT",EDGE,{"disambiguationData":[TD([[subQ5,-1.0]])],"derivedFrom":subQ0}),1.0]])]});}
            var Q26;
            {var subQ0=sQuery(id+"F0.wireOp",EDGE,"E148.MirrorCS");Q26=makeQuery(id+"F0.imprint","IMPRINT",FACE,{"disambiguationData":[TD([[makeQuery(id+"F0.imprint","IMPRINT",EDGE,{"derivedFrom":subQ0}),-1.0]])]});}
            var Q27;
            {var subQ17=sQuery(id+"F0.wireOp",EDGE,"E96.MirrorCS");Q27=makeQuery(id+"F0.imprint","IMPRINT",FACE,{"disambiguationData":[TD([[makeQuery(id+"F0.imprint","IMPRINT",EDGE,{"derivedFrom":subQ17}),-1.0]])]});}
            var Q28;
            {var subQ0=sQuery(id+"F0.wireOp",EDGE,"E162.MirrorCS");Q28=makeQuery(id+"F0.imprint","IMPRINT",FACE,{"disambiguationData":[TD([[makeQuery(id+"F0.imprint","IMPRINT",EDGE,{"derivedFrom":subQ0}),-1.0]])]});}
            var Q29;
            {var subQ0=sQuery(id+"F0.wireOp",EDGE,"E101.MirrorCS");Q29=makeQuery(id+"F0.imprint","IMPRINT",FACE,{"disambiguationData":[TD([[makeQuery(id+"F0.imprint","IMPRINT",EDGE,{"derivedFrom":subQ0}),-1.0]])]});}
            var Q30;
            {var subQ2=sQuery(id+"F0.wireOp",EDGE,"E53");Q30=makeQuery(id+"F0.imprint","IMPRINT",FACE,{"disambiguationData":[TD([[makeQuery(id+"F0.imprint","IMPRINT",EDGE,{"derivedFrom":subQ2}),-1.0]])]});}
            var Q31;
            {var subQ2=sQuery(id+"F0.wireOp",EDGE,"E200");var subQ6=sQuery(id+"F0.wireOp",EDGE,"E203");var subQ8=makeQuery(id+"F0.imprint","INTERSECT",VERTEX,{"derivedFrom":[subQ2,subQ6]});Q31=makeQuery(id+"F0.imprint","IMPRINT",FACE,{"disambiguationData":[TD([[makeQuery(id+"F0.imprint","IMPRINT",EDGE,{"disambiguationData":[TD([[subQ8,-1.0]])],"derivedFrom":subQ2}),1.0]])]});}
            var Q32;
            {var subQ4=sQuery(id+"F0.wireOp",EDGE,"E200");var subQ6=sQuery(id+"F0.wireOp",EDGE,"E203");var subQ7=makeQuery(id+"F0.imprint","INTERSECT",VERTEX,{"derivedFrom":[subQ4,subQ6]});Q32=makeQuery(id+"F0.imprint","IMPRINT",FACE,{"disambiguationData":[TD([[makeQuery(id+"F0.imprint","IMPRINT",EDGE,{"disambiguationData":[TD([[subQ7,-1.0]])],"derivedFrom":subQ4}),-1.0]])]});}
            var Q33;
            {var subQ0=sQuery(id+"F0.wireOp",EDGE,"E72.trimOffspring");var subQ1=sQuery(id+"F0.wireOp",EDGE,"E71.MirrorCS");var subQ2=makeQuery(id+"F0.imprint","INTERSECT",VERTEX,{"derivedFrom":[subQ1,subQ0]});Q33=makeQuery(id+"F0.imprint","IMPRINT",FACE,{"disambiguationData":[TD([[makeQuery(id+"F0.imprint","IMPRINT",EDGE,{"disambiguationData":[TD([[subQ2,-1.0]])],"derivedFrom":subQ1}),-1.0]])]});}
            var Q34;
            {var subQ0=sQuery(id+"F0.wireOp",EDGE,"E173.MirrorCS");Q34=makeQuery(id+"F0.imprint","IMPRINT",FACE,{"disambiguationData":[TD([[makeQuery(id+"F0.imprint","IMPRINT",EDGE,{"derivedFrom":subQ0}),1.0]])]});}
            var Q35;
            {var subQ3=sQuery(id+"F0.wireOp",EDGE,"E170.MirrorCS");var subQ5=sQuery(id+"F0.wireOp",EDGE,"E228");var subQ7=makeQuery(id+"F0.imprint","INTERSECT",VERTEX,{"derivedFrom":[subQ3,subQ5]});Q35=makeQuery(id+"F0.imprint","IMPRINT",FACE,{"disambiguationData":[TD([[makeQuery(id+"F0.imprint","IMPRINT",EDGE,{"disambiguationData":[TD([[subQ7,1.0]])],"derivedFrom":subQ5}),-1.0]])]});}
            var Q36;
            {var subQ3=sQuery(id+"F0.wireOp",EDGE,"E229");var subQ5=sQuery(id+"F0.wireOp",EDGE,"E3");var subQ7=makeQuery(id+"F0.imprint","INTERSECT",VERTEX,{"derivedFrom":[subQ5,subQ3]});Q36=makeQuery(id+"F0.imprint","IMPRINT",FACE,{"disambiguationData":[TD([[makeQuery(id+"F0.imprint","IMPRINT",EDGE,{"disambiguationData":[TD([[subQ7,-1.0]])],"derivedFrom":subQ3}),-1.0]])]});}
            var Q37;
            {var subQ1=sQuery(id+"F0.wireOp",EDGE,"E2");var subQ3=sQuery(id+"F0.wireOp",EDGE,"E229");var subQ4=makeQuery(id+"F0.imprint","INTERSECT",VERTEX,{"derivedFrom":[subQ1,subQ3]});Q37=makeQuery(id+"F0.imprint","IMPRINT",FACE,{"disambiguationData":[TD([[makeQuery(id+"F0.imprint","IMPRINT",EDGE,{"disambiguationData":[TD([[subQ4,-1.0]])],"derivedFrom":subQ3}),-1.0]])]});}
            var Q38;
            {var subQ33=sQuery(id+"F0.wireOp",EDGE,"E0.left");Q38=makeQuery(id+"F0.imprint","IMPRINT",FACE,{"disambiguationData":[TD([[makeQuery(id+"F0.imprint","IMPRINT",EDGE,{"derivedFrom":subQ33}),1.0]])]});}
            extrude(context, id + "F1", {"entities" : qUnion([Q0, Q1, Q2, Q3, Q4, Q5, Q6, Q7, Q8, Q9, Q10, Q11, Q12, Q13, Q14, Q15, Q16, Q17, Q18, Q19, Q20, Q21, Q22, Q23, Q24, Q25, Q26, Q27, Q28, Q29, Q30, Q31, Q32, Q33, Q34, Q35, Q36, Q37, Q38]), "depth" : 3 * mm});
        }
    });
